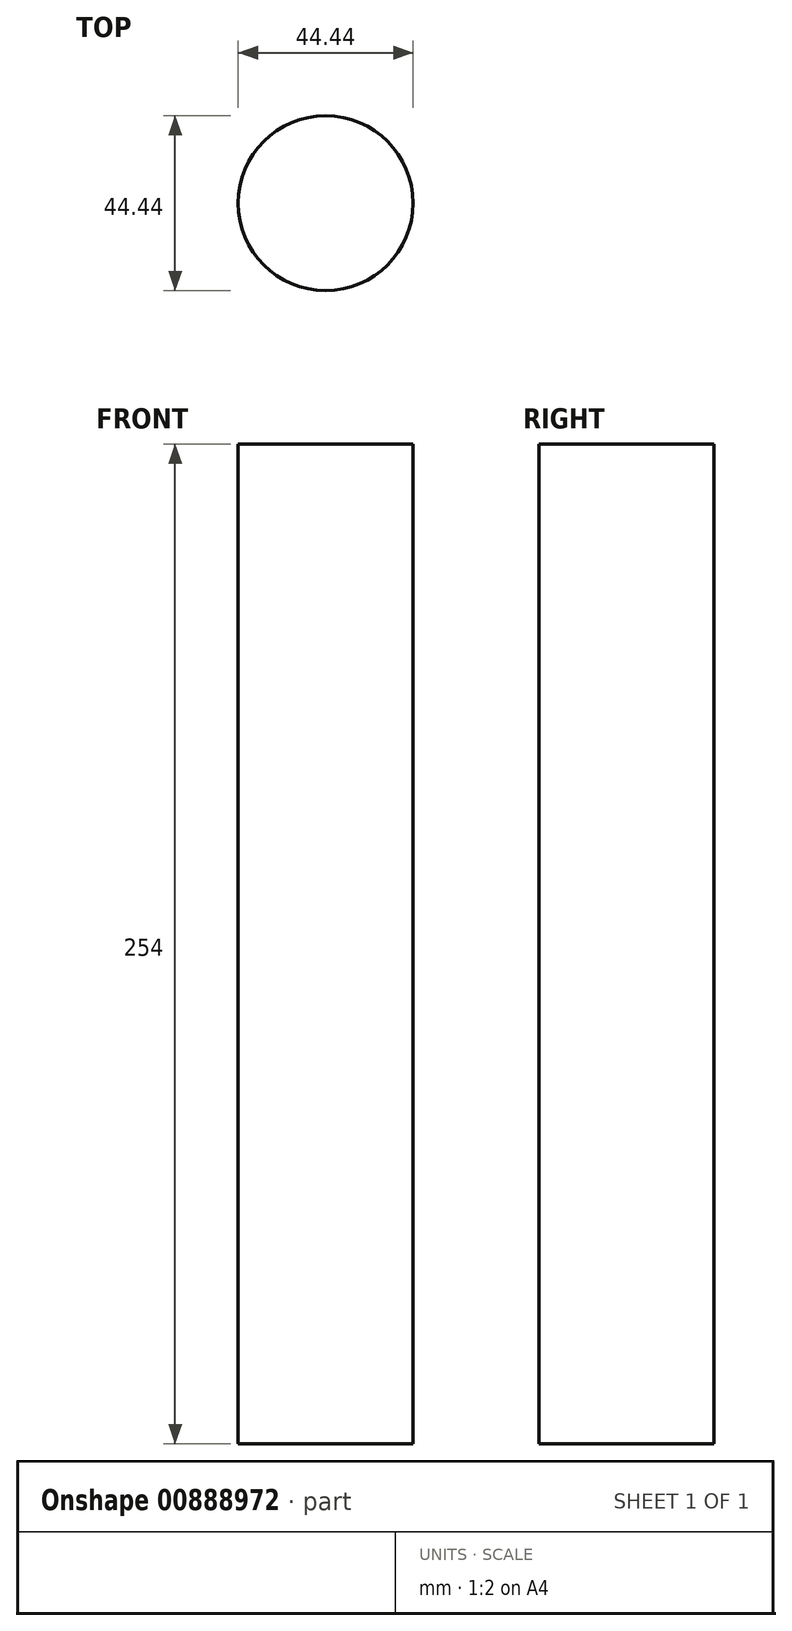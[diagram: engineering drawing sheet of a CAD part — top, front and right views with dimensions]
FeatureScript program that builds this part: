
annotation { "Feature Type Name" : "Feature", "Feature Type Description" : "" }
export const myFeature = defineFeature(function(context is Context, id is Id, definition is map)
    precondition{}
    {
        {
            var Q0;
            Q0=qCreatedBy(makeId("Top.planeOp"),FACE);
            var sketch = newSketch(context, id + "F0", { "sketchPlane" : qUnion([Q0])});
            skCircle(sketch, "E0", {"center": v(0, 0) * mm, "radius": 22.22 * mm});
            skSolve(sketch);
        }
        {
            var Q0;
            Q0=makeQuery(id+"F0.imprint","IMPRINT",FACE,{"disambiguationData":[TD([[makeQuery(id+"F0.imprint","IMPRINT",EDGE,{"derivedFrom":sQuery(id+"F0.wireOp",EDGE,"E0")}),1.0]])]});
            extrude(context, id + "F1", {"entities" : qUnion([Q0]), "depth" : 254 * mm, "offsetDistance" : 25.4 * mm});
        }
    });
